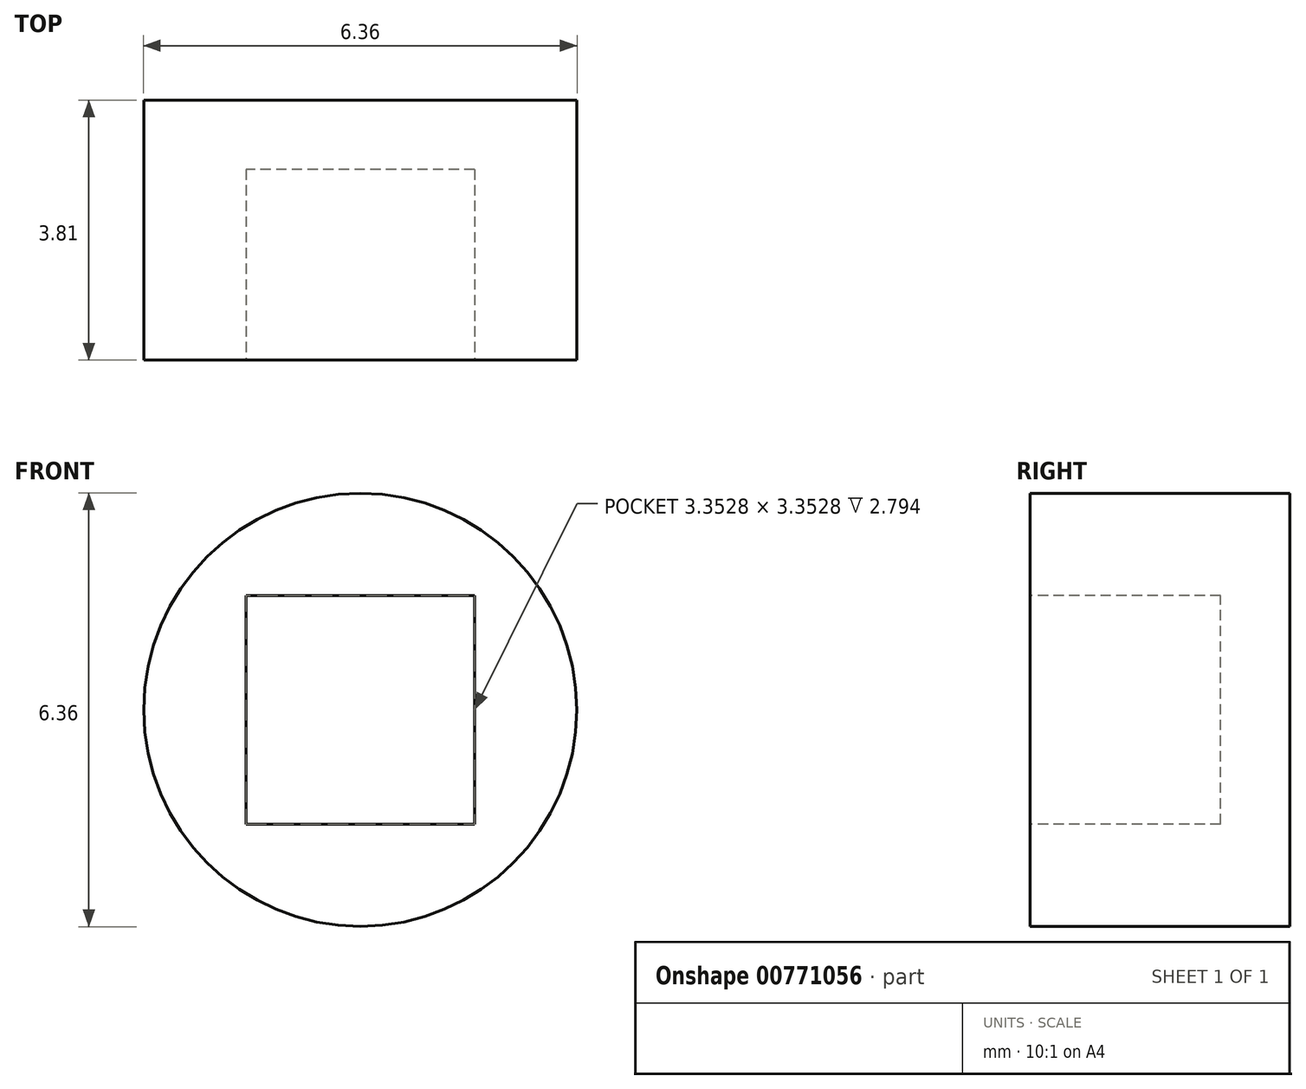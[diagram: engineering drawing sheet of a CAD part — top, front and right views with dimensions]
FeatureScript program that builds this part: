
annotation { "Feature Type Name" : "Feature", "Feature Type Description" : "" }
export const myFeature = defineFeature(function(context is Context, id is Id, definition is map)
    precondition{}
    {
        {
            var Q0;
            Q0=qCreatedBy(makeId("Front.planeOp"),FACE);
            var sketch = newSketch(context, id + "F0", { "sketchPlane" : qUnion([Q0])});
            skCircle(sketch, "E0", {"center": v(0, 0) * mm, "radius": 3.18 * mm});
            skSolve(sketch);
        }
        {
            var Q0;
            Q0=makeQuery(id+"F0.imprint","IMPRINT",FACE,{"disambiguationData":[TD([[makeQuery(id+"F0.imprint","IMPRINT",EDGE,{"derivedFrom":sQuery(id+"F0.wireOp",EDGE,"E0")}),1.0]])]});
            extrude(context, id + "F1", {"entities" : qUnion([Q0]), "depth" : 3.8 * mm, "offsetDistance" : 25.4 * mm});
        }
        {
            var Q0;
            Q0=makeQuery(id+"F1.opExtrude","CAP_FACE",FACE,{"disambiguationData":[OSD([sQuery(id+"F0.wireOp",EDGE,"E0")])],"isStart":false});
            var sketch = newSketch(context, id + "F2", { "sketchPlane" : qUnion([Q0])});
            skLineSegment(sketch, "E1.bottom", {"start": v(1.68, -1.68) * mm, "end": v(-1.68, -1.68) * mm});
            skLineSegment(sketch, "E1.top", {"start": v(1.68, 1.68) * mm, "end": v(-1.68, 1.68) * mm});
            skLineSegment(sketch, "E1.left", {"start": v(1.68, -1.68) * mm, "end": v(1.68, 1.68) * mm});
            skLineSegment(sketch, "E1.right", {"start": v(-1.68, -1.68) * mm, "end": v(-1.68, 1.68) * mm});
            skPoint(sketch, "E1.middle", {"position": v(0, 0) * mm});
            skSolve(sketch);
        }
        {
            var Q0;
            Q0=makeQuery(id+"F2.imprint","IMPRINT",FACE,{"disambiguationData":[TD([[makeQuery(id+"F2.imprint","IMPRINT",EDGE,{"derivedFrom":sQuery(id+"F2.wireOp",EDGE,"E1.bottom")}),-1.0]])]});
            extrude(context, id + "F3", {"entities" : qUnion([Q0]), "operationType" : NewBodyOperationType.REMOVE, "oppositeDirection" : true, "depth" : 2.8 * mm, "offsetDistance" : 25.4 * mm});
        }
    });
